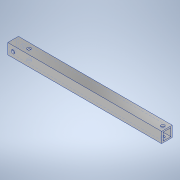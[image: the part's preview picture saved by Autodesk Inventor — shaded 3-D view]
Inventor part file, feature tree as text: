
AUTODESK INVENTOR PART (.ipt)
format: ipt  version: 2020.3 (Build 243373000, 373)  size: 133,120 bytes
history: native  units: mm
features: sketch x3, hole x2, other x1, extrude x1
ambient origin geometry x8: Origin, YZ Plane, XZ Plane, XY Plane, X Axis, Y Axis, Z Axis, Center Point
bodies: Body1 (feature_tree)
feature tree (7):
  other  "ソリッド1"
  extrude  "押し出し1"  Depth=9.0mm
  hole  "穴1"  [1 undecoded]
  hole  "穴2"  [1 undecoded]
  sketch  "スケッチ1"
  sketch  "スケッチ2"
  sketch  "スケッチ3"
note: 2 required parameter values undecoded (feature->parameter linkage not recoverable at this tier; creation-order binding heuristic only, values carry confidence <= 0.55)
